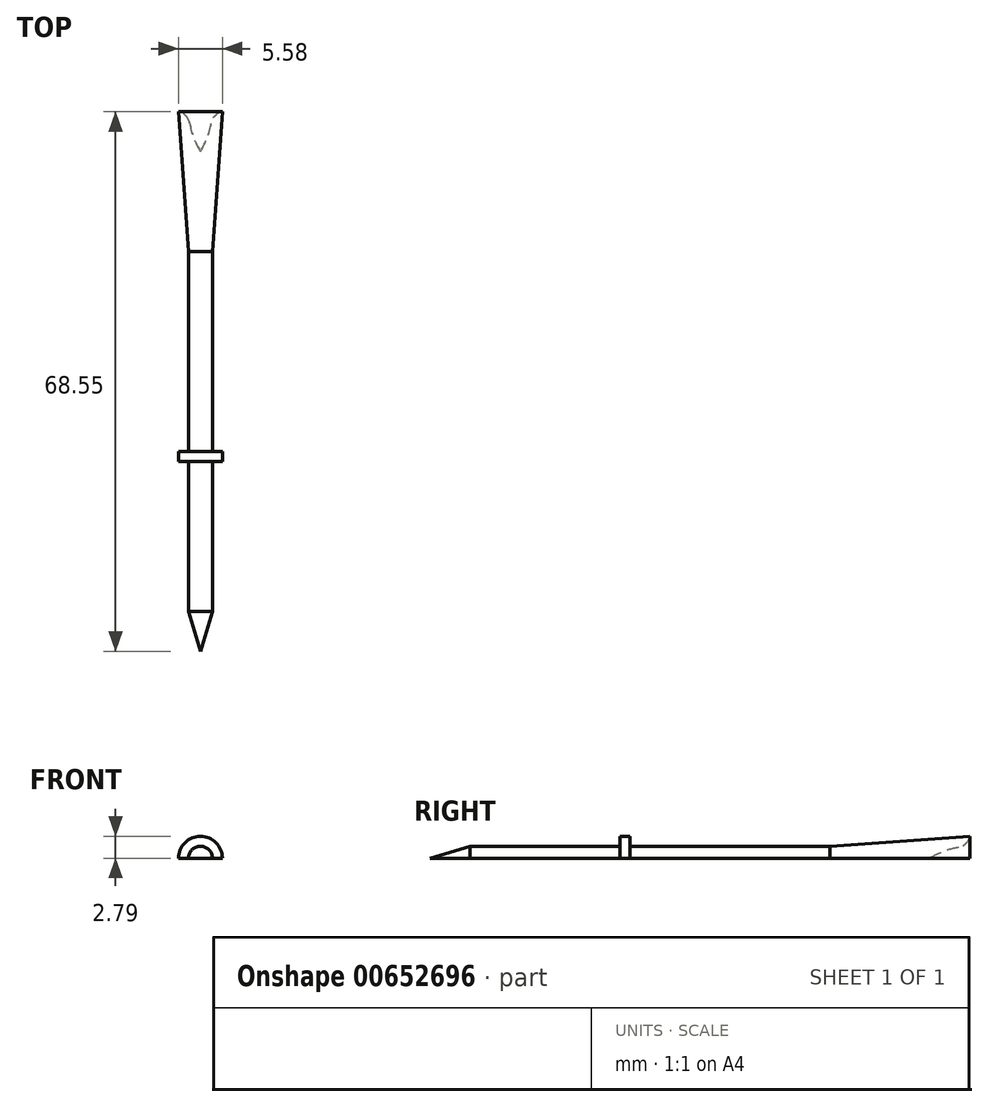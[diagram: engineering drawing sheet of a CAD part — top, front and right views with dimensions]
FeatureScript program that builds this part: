
annotation { "Feature Type Name" : "Feature", "Feature Type Description" : "" }
export const myFeature = defineFeature(function(context is Context, id is Id, definition is map)
    precondition{}
    {
        {
            var Q0;
            Q0=qCreatedBy(makeId("Top.planeOp"),FACE);
            var sketch = newSketch(context, id + "F0", { "sketchPlane" : qUnion([Q0])});
            skLineSegment(sketch, "E0", {"start": v(0, 0) * mm, "end": v(0, 63.5) * mm});
            skArc(sketch, "E1", {"start": v(-1.38, 67.1) * mm, "mid": v(-0.86, 65.24) * mm, "end": v(0, 63.5) * mm});
            skLineSegment(sketch, "E2", {"start": v(-2.8, 68.58) * mm, "end": v(-3.13, 68.58) * mm});
            skLineSegment(sketch, "E3", {"start": v(-1.52, 5.08) * mm, "end": v(0, 0) * mm});
            skLineSegment(sketch, "E4", {"start": v(-1.52, 5.08) * mm, "end": v(-1.52, 24.13) * mm});
            skLineSegment(sketch, "E5", {"start": v(-1.52, 50.8) * mm, "end": v(-2.8, 68.58) * mm});
            skLineSegment(sketch, "E6", {"start": v(-1.52, 25.4) * mm, "end": v(-2.8, 25.4) * mm});
            skLineSegment(sketch, "E7", {"start": v(-2.8, 25.4) * mm, "end": v(-2.8, 24.13) * mm});
            skLineSegment(sketch, "E8", {"start": v(-2.8, 24.13) * mm, "end": v(-1.52, 24.13) * mm});
            skLineSegment(sketch, "E9.trimOffspring", {"start": v(-1.52, 25.4) * mm, "end": v(-1.52, 50.8) * mm});
            skPoint(sketch, "E10.visualSharp", {"position": v(-1.52, 68.58) * mm});
            skArc(sketch, "E10.filletArc", {"start": v(-1.38, 67.1) * mm, "mid": v(-1.98, 68.16) * mm, "end": v(-3.13, 68.58) * mm});
            skSolve(sketch);
        }
        {
            var Q0;
            Q0=makeQuery(id+"F0.imprint","IMPRINT",FACE,{"disambiguationData":[TD([[makeQuery(id+"F0.imprint","IMPRINT",EDGE,{"derivedFrom":sQuery(id+"F0.wireOp",EDGE,"E0")}),1.0]])]});
            var Q1;
            Q1=sQuery(id+"F0.wireOp",EDGE,"E0");
            revolve(context, id + "F1", {"entities" : qUnion([Q0]), "axis" : qUnion([Q1]), "revolveType" : RevolveType.ONE_DIRECTION, "angle" : 180 * degree});
        }
    });
